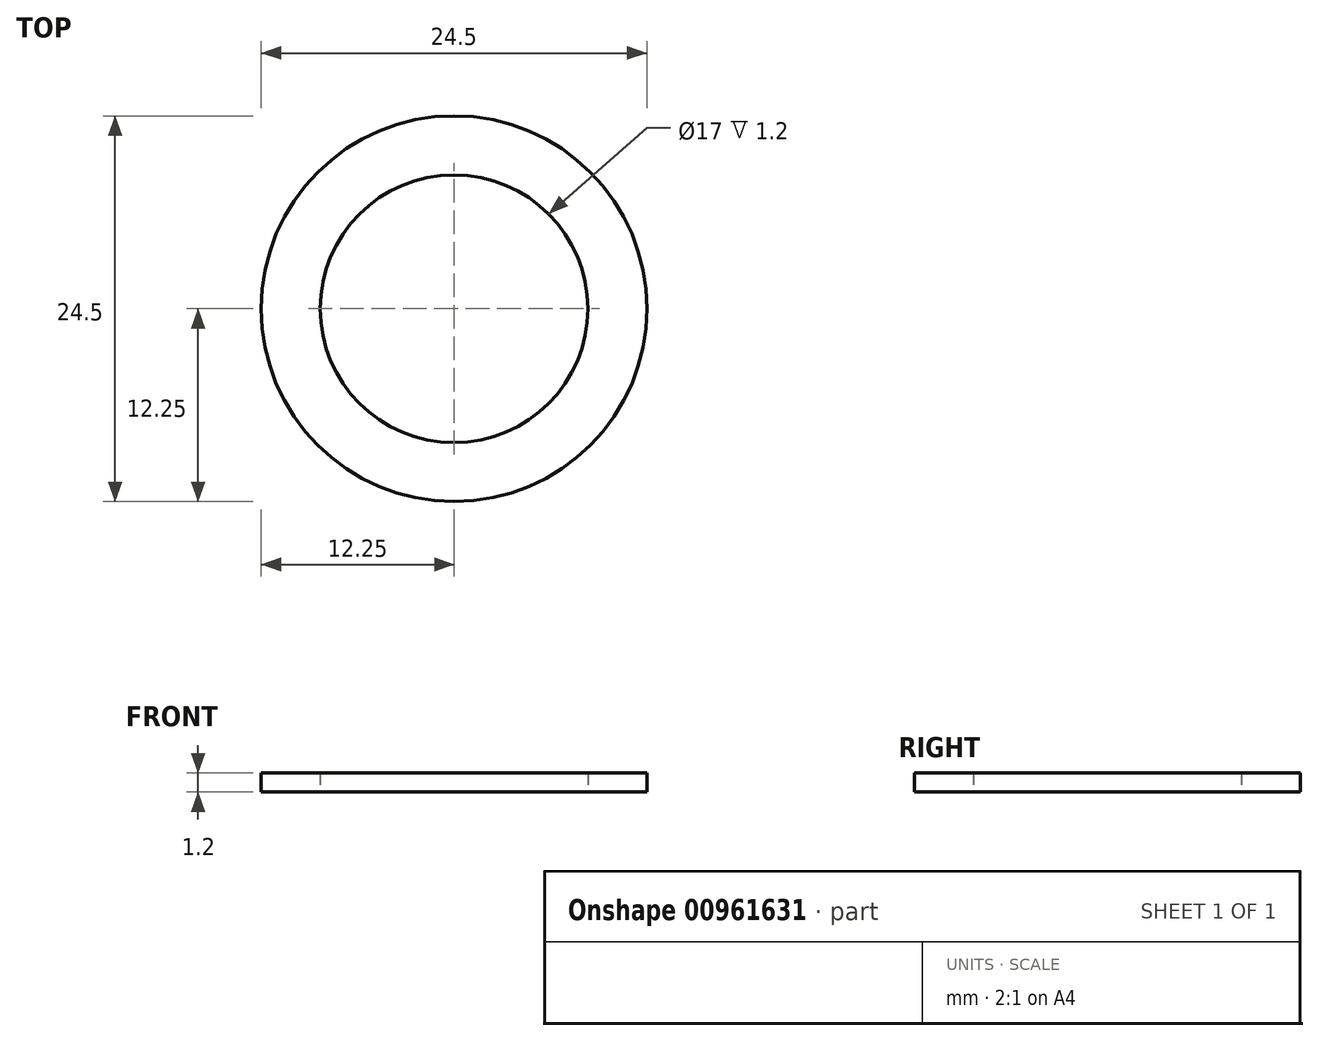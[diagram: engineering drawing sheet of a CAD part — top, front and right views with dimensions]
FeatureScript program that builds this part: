
annotation { "Feature Type Name" : "Feature", "Feature Type Description" : "" }
export const myFeature = defineFeature(function(context is Context, id is Id, definition is map)
    precondition{}
    {
        {
            var Q0;
            Q0=qCreatedBy(makeId("Top.planeOp"),FACE);
            var sketch = newSketch(context, id + "F0", { "sketchPlane" : qUnion([Q0])});
            skCircle(sketch, "E0", {"center": v(0, 0) * mm, "radius": 12.25 * mm});
            skCircle(sketch, "E1", {"center": v(0, 0) * mm, "radius": 8.5 * mm});
            skSolve(sketch);
        }
        {
            var Q0;
            Q0 = qSketchRegion(id + "F0", true);
            extrude(context, id + "F1", {"entities" : qUnion([Q0]), "depth" : 1.2 * mm, "offsetDistance" : 25 * mm});
        }
    });
